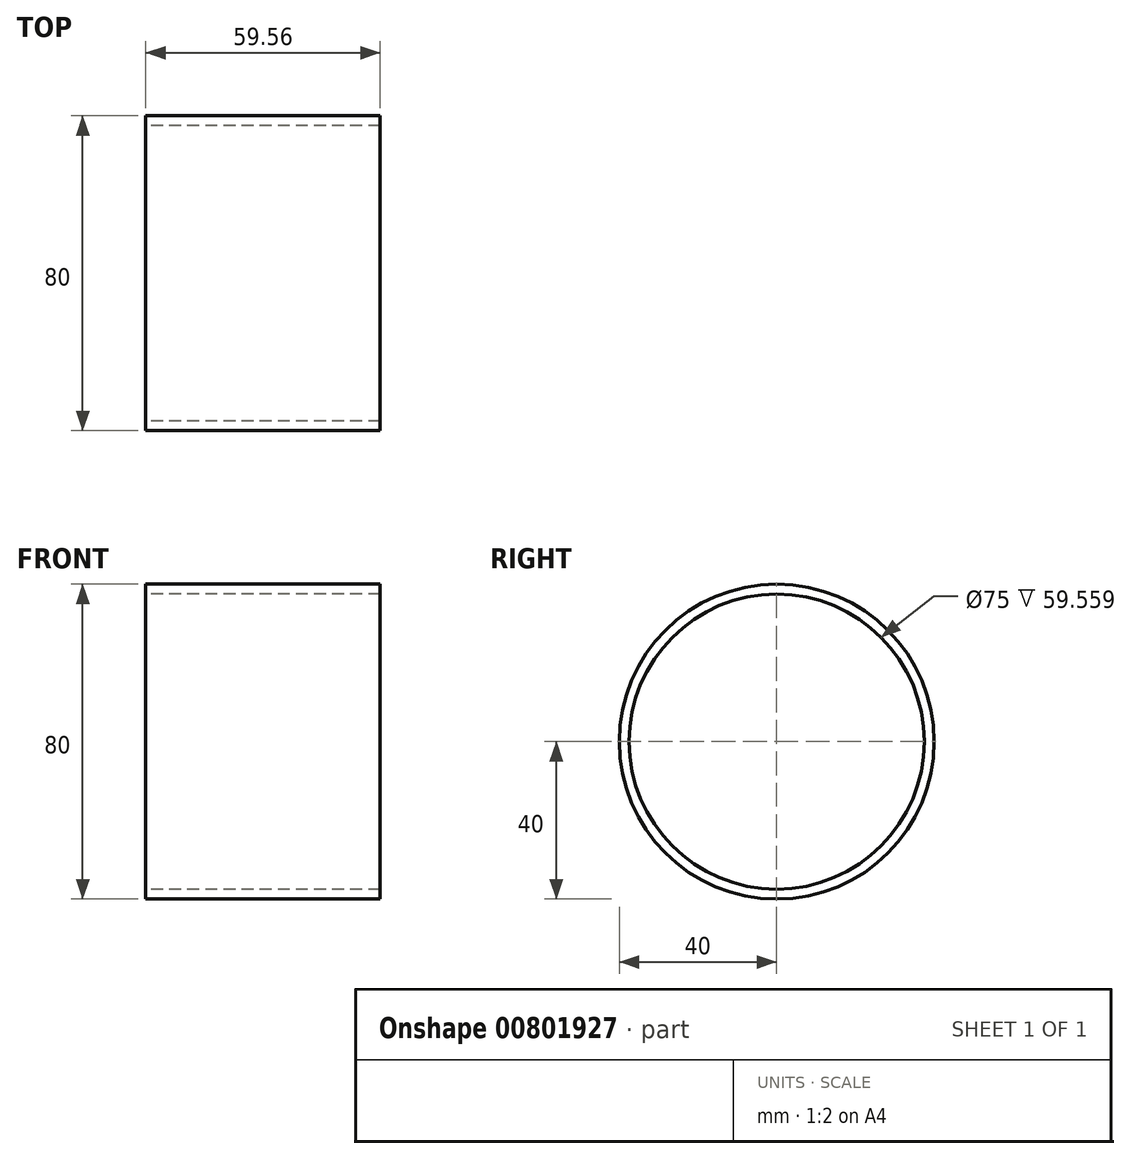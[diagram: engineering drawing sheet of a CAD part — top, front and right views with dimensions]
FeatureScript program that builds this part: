
annotation { "Feature Type Name" : "Feature", "Feature Type Description" : "" }
export const myFeature = defineFeature(function(context is Context, id is Id, definition is map)
    precondition{}
    {
        {
            var Q0;
            Q0=qCreatedBy(makeId("Right.planeOp"),FACE);
            var sketch = newSketch(context, id + "F0", { "sketchPlane" : qUnion([Q0])});
            skCircle(sketch, "E0", {"center": v(0, 0) * mm, "radius": 37.5 * mm});
            skCircle(sketch, "E1", {"center": v(0, 0) * mm, "radius": 40 * mm});
            skSolve(sketch);
        }
        {
            var Q0;
            Q0=qSketchRegion(id+"F0",true);
            extrude(context, id + "F1", {"entities" : qUnion([Q0]), "depth" : 59.56 * mm});
        }
    });
